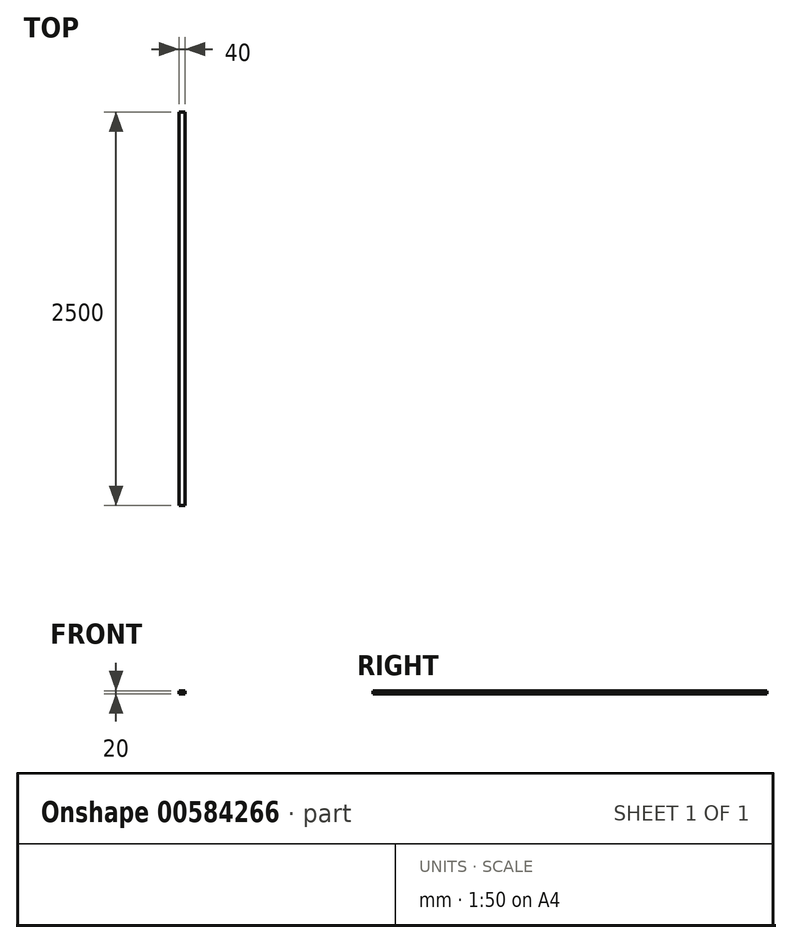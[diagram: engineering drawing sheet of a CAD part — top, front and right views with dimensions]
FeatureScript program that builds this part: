
annotation { "Feature Type Name" : "Feature", "Feature Type Description" : "" }
export const myFeature = defineFeature(function(context is Context, id is Id, definition is map)
    precondition{}
    {
        {
            var Q0;
            Q0=qCreatedBy(makeId("Front.planeOp"),FACE);
            var sketch = newSketch(context, id + "F0", { "sketchPlane" : qUnion([Q0])});
            skLineSegment(sketch, "E0.bottom", {"start": v(0, 0) * mm, "end": v(40, 0) * mm});
            skLineSegment(sketch, "E0.top", {"start": v(0, 20) * mm, "end": v(40, 20) * mm});
            skLineSegment(sketch, "E0.left", {"start": v(0, 0) * mm, "end": v(0, 20) * mm});
            skLineSegment(sketch, "E0.right", {"start": v(40, 0) * mm, "end": v(40, 20) * mm});
            skSolve(sketch);
        }
        {
            var Q0;
            Q0=makeQuery(id+"F0.imprint","IMPRINT",FACE,{"disambiguationData":[TD([[makeQuery(id+"F0.imprint","IMPRINT",EDGE,{"derivedFrom":sQuery(id+"F0.wireOp",EDGE,"E0.bottom")}),1.0]])]});
            extrude(context, id + "F1", {"entities" : qUnion([Q0]), "depth" : 2500 * mm, "offsetDistance" : 25 * mm});
        }
    });
